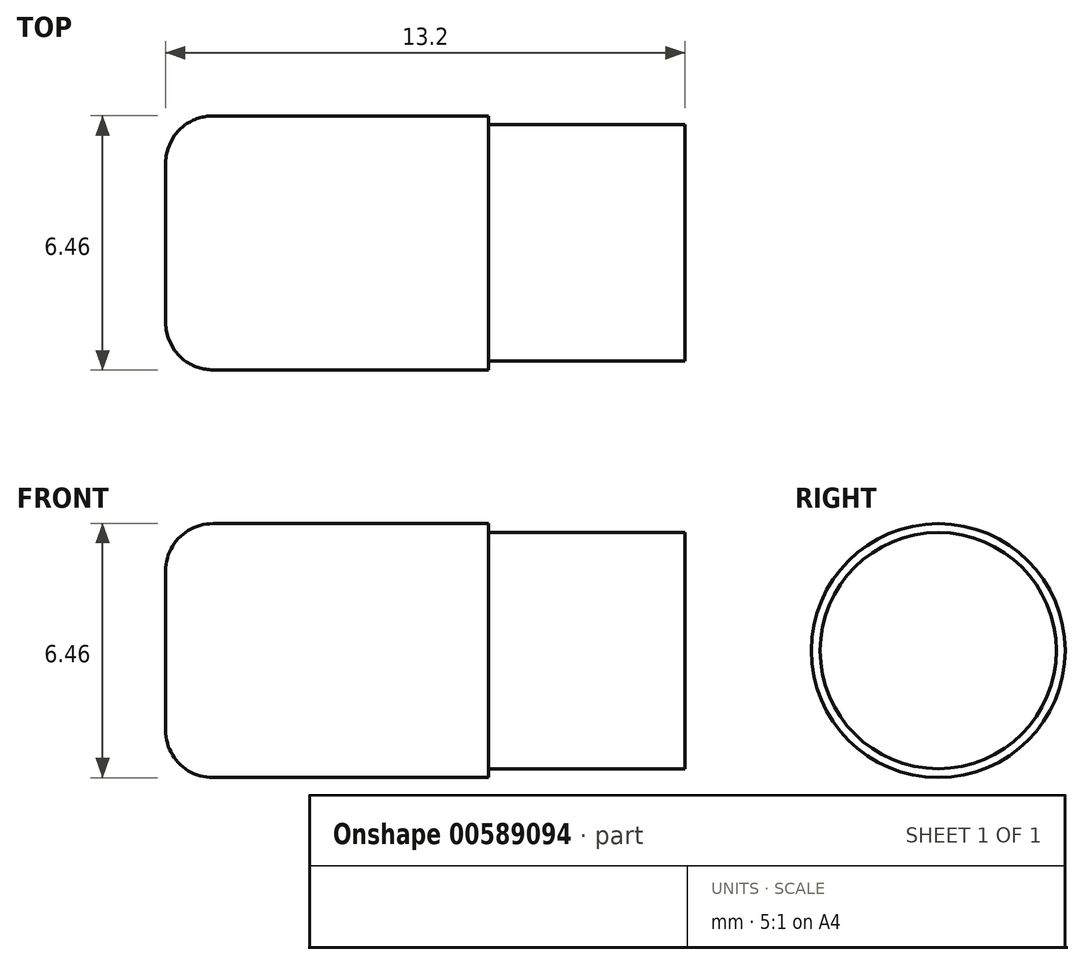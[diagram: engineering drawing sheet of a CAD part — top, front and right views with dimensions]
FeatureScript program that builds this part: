
annotation { "Feature Type Name" : "Feature", "Feature Type Description" : "" }
export const myFeature = defineFeature(function(context is Context, id is Id, definition is map)
    precondition{}
    {
        {
            var Q0;
            Q0=qCreatedBy(makeId("Front.planeOp"),FACE);
            var sketch = newSketch(context, id + "F0", { "sketchPlane" : qUnion([Q0])});
            skLineSegment(sketch, "E0.bottom", {"start": v(-7, 3.23) * mm, "end": v(0, 3.23) * mm});
            skLineSegment(sketch, "E0.top", {"start": v(-8.2, 0) * mm, "end": v(5, 0) * mm});
            skLineSegment(sketch, "E0.left", {"start": v(-8.2, 2.03) * mm, "end": v(-8.2, 0) * mm});
            skLineSegment(sketch, "E0.right", {"start": v(5, 3) * mm, "end": v(5, 0) * mm});
            skLineSegment(sketch, "E1", {"start": v(0, 3.22) * mm, "end": v(0, 3) * mm});
            skLineSegment(sketch, "E2", {"start": v(0, 3) * mm, "end": v(5, 3) * mm});
            skPoint(sketch, "E3.visualSharp", {"position": v(-8.2, 3.23) * mm});
            skArc(sketch, "E3.filletArc", {"start": v(-7, 3.23) * mm, "mid": v(-7.85, 2.87) * mm, "end": v(-8.2, 2.03) * mm});
            skSolve(sketch);
        }
        {
            var Q0;
            Q0 = qSketchRegion(id + "F0", true);
            var Q1;
            Q1=sQuery(id+"F0.wireOp",EDGE,"E0.top");
            revolve(context, id + "F1", {"entities" : qUnion([Q0]), "axis" : qUnion([Q1]), "revolveType" : RevolveType.FULL});
        }
    });
